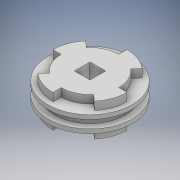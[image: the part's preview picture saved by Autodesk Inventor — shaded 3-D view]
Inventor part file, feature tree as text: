
AUTODESK INVENTOR PART (.ipt)
format: ipt  version: 2017 (Build 210142000, 142)  size: 193,024 bytes
history: native  units: mm
features: extrude x4, sketch x4, plane x1, pattern_circular x1, mirror x1, projected_geometry x1
ambient origin geometry x8: Origin, YZ Plane, XZ Plane, XY Plane, X Axis, Y Axis, Z Axis, Center Point
bodies: Solid1 (feature_tree)
feature tree (12):
  extrude  "Extrusion1"  Depth=8.0mm
  plane  "Work Plane1"
  extrude  "Extrusion2"  Depth=10.0mm
  extrude  "Extrusion3"  Depth=5.0mm
  pattern_circular  "Circular Pattern1"  [2 undecoded]
  mirror  "Mirror1"
  extrude  "Extrusion4"  Depth=10.0mm TaperAngle=360.0deg
  sketch  "Sketch1"  dims[d0=35.0mm d1=8.0mm]
  sketch  "Sketch2"  dims[d2=10.0mm d3=0.0mm d4=4.0mm]
  sketch  "Sketch3"  dims[d5=5.0mm d6=0.0mm d7=5.0mm]
  sketch  "Sketch4"  dims[d8=6.981317mm d9=5.0mm d10=0.0mm d11=40.0mm d12=360.0deg d14=9.525mm d15=10.0mm d16=0.0mm]
  projected_geometry  "Projected Loop1"
note: 2 required parameter values undecoded (feature->parameter linkage not recoverable at this tier; creation-order binding heuristic only, values carry confidence <= 0.55)
